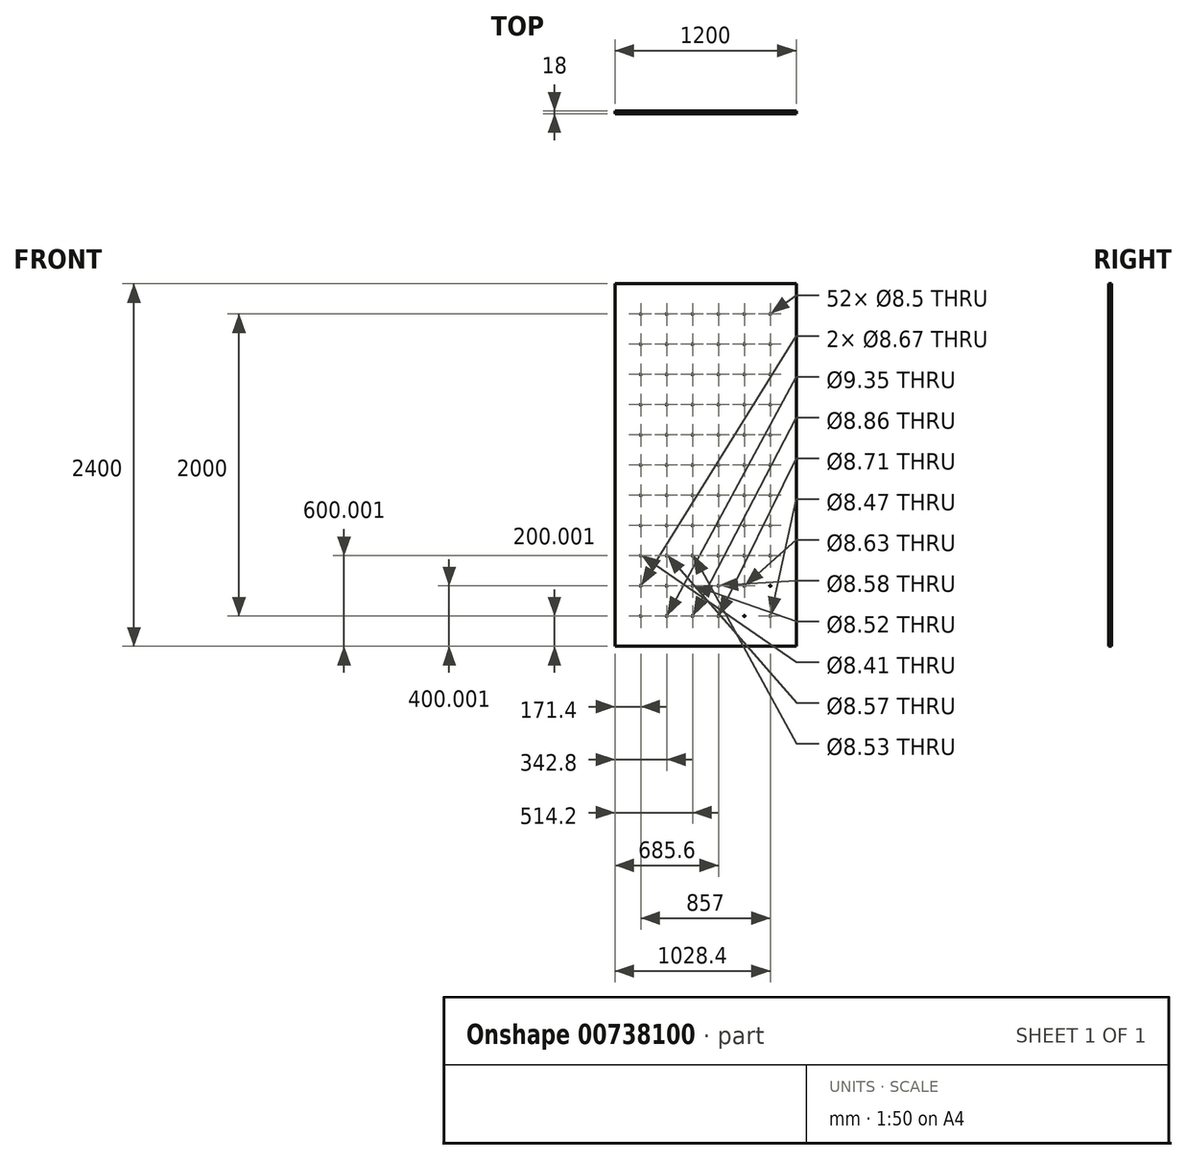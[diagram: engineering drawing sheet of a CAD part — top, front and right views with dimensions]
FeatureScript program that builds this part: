
annotation { "Feature Type Name" : "Feature", "Feature Type Description" : "" }
export const myFeature = defineFeature(function(context is Context, id is Id, definition is map)
    precondition{}
    {
        {
            var Q0;
            Q0=qCreatedBy(makeId("Front.planeOp"),FACE);
            var sketch = newSketch(context, id + "F0", { "sketchPlane" : qUnion([Q0])});
            skLineSegment(sketch, "E0.bottom", {"start": v(-600, 1570.02) * mm, "end": v(600, 1570.02) * mm});
            skLineSegment(sketch, "E0.top", {"start": v(-600, -829.98) * mm, "end": v(600, -829.98) * mm});
            skLineSegment(sketch, "E0.left", {"start": v(-600, 1570.02) * mm, "end": v(-600, -829.98) * mm});
            skLineSegment(sketch, "E0.right", {"start": v(600, 1570.02) * mm, "end": v(600, -829.98) * mm});
            skPoint(sketch, "E1", {"position": v(-428.6, 1570.02) * mm});
            skPoint(sketch, "E2", {"position": v(-257.2, 1570.02) * mm});
            skPoint(sketch, "E3", {"position": v(-85.8, 1570.02) * mm});
            skPoint(sketch, "E4", {"position": v(257, 1570.02) * mm});
            skPoint(sketch, "E5", {"position": v(428.4, 1570.02) * mm});
            skPoint(sketch, "E6", {"position": v(85.6, 1570.02) * mm});
            skPoint(sketch, "E7", {"position": v(-600, 1370.02) * mm});
            skPoint(sketch, "E8", {"position": v(-600, 1170.02) * mm});
            skPoint(sketch, "E9", {"position": v(-600, 970.02) * mm});
            skPoint(sketch, "E10", {"position": v(-600, 770.02) * mm});
            skPoint(sketch, "E11", {"position": v(-600, 570.02) * mm});
            skPoint(sketch, "E12", {"position": v(-600, 370.02) * mm});
            skPoint(sketch, "E13", {"position": v(-600, 170.02) * mm});
            skPoint(sketch, "E14", {"position": v(-600, -29.98) * mm});
            skPoint(sketch, "E15", {"position": v(-600, -229.98) * mm});
            skPoint(sketch, "E16", {"position": v(-600, -429.98) * mm});
            skPoint(sketch, "E17", {"position": v(-600, -629.98) * mm});
            skPoint(sketch, "E18.endSnap0", {"position": v(0, -829.98) * mm});
            skCircle(sketch, "E19", {"center": v(-428.6, -629.98) * mm, "radius": 4.25 * mm});
            skCircle(sketch, "E20", {"center": v(-257.2, -629.98) * mm, "radius": 4.67 * mm});
            skCircle(sketch, "E21", {"center": v(-85.8, -629.98) * mm, "radius": 4.43 * mm});
            skCircle(sketch, "E22", {"center": v(85.6, -629.98) * mm, "radius": 4.35 * mm});
            skCircle(sketch, "E23", {"center": v(257, -629.98) * mm, "radius": 4.1 * mm});
            skCircle(sketch, "E24", {"center": v(428.4, -629.98) * mm, "radius": 4.23 * mm});
            skCircle(sketch, "E25", {"center": v(428.4, -429.98) * mm, "radius": 4.2 * mm});
            skCircle(sketch, "E26", {"center": v(257, -429.98) * mm, "radius": 4.32 * mm});
            skCircle(sketch, "E27", {"center": v(85.6, -429.98) * mm, "radius": 4.29 * mm});
            skCircle(sketch, "E28", {"center": v(-85.8, -429.98) * mm, "radius": 4.26 * mm});
            skCircle(sketch, "E29", {"center": v(-257.2, -429.98) * mm, "radius": 4.33 * mm});
            skCircle(sketch, "E30", {"center": v(-428.6, -429.98) * mm, "radius": 4.33 * mm});
            skCircle(sketch, "E31", {"center": v(-428.6, -229.98) * mm, "radius": 4.2 * mm});
            skCircle(sketch, "E32", {"center": v(-257.2, -229.98) * mm, "radius": 4.29 * mm});
            skCircle(sketch, "E33", {"center": v(-85.8, -229.98) * mm, "radius": 4.26 * mm});
            skCircle(sketch, "E34", {"center": v(85.6, -229.98) * mm, "radius": 4.25 * mm});
            skCircle(sketch, "E35", {"center": v(257, -229.98) * mm, "radius": 4.25 * mm});
            skCircle(sketch, "E36", {"center": v(428.4, -229.98) * mm, "radius": 4.25 * mm});
            skCircle(sketch, "E37", {"center": v(428.4, -29.98) * mm, "radius": 4.25 * mm});
            skCircle(sketch, "E38", {"center": v(257, -29.98) * mm, "radius": 4.25 * mm});
            skCircle(sketch, "E39", {"center": v(85.6, -29.98) * mm, "radius": 4.25 * mm});
            skCircle(sketch, "E40", {"center": v(-85.8, -29.98) * mm, "radius": 4.25 * mm});
            skCircle(sketch, "E41", {"center": v(-257.2, -29.98) * mm, "radius": 4.25 * mm});
            skCircle(sketch, "E42", {"center": v(-428.6, -29.98) * mm, "radius": 4.25 * mm});
            skCircle(sketch, "E43", {"center": v(428.4, 170.02) * mm, "radius": 4.25 * mm});
            skCircle(sketch, "E44", {"center": v(257, 170.02) * mm, "radius": 4.25 * mm});
            skCircle(sketch, "E45", {"center": v(85.6, 170.02) * mm, "radius": 4.25 * mm});
            skCircle(sketch, "E46", {"center": v(-85.8, 170.02) * mm, "radius": 4.25 * mm});
            skCircle(sketch, "E47", {"center": v(-257.2, 170.02) * mm, "radius": 4.25 * mm});
            skCircle(sketch, "E48", {"center": v(-428.6, 170.02) * mm, "radius": 4.25 * mm});
            skCircle(sketch, "E49", {"center": v(-428.6, 370.02) * mm, "radius": 4.25 * mm});
            skCircle(sketch, "E50", {"center": v(-257.2, 370.02) * mm, "radius": 4.25 * mm});
            skCircle(sketch, "E51", {"center": v(-85.8, 370.02) * mm, "radius": 4.25 * mm});
            skCircle(sketch, "E52", {"center": v(85.6, 370.02) * mm, "radius": 4.25 * mm});
            skCircle(sketch, "E53", {"center": v(257, 370.02) * mm, "radius": 4.25 * mm});
            skCircle(sketch, "E54", {"center": v(428.4, 370.02) * mm, "radius": 4.25 * mm});
            skCircle(sketch, "E55", {"center": v(428.4, 570.02) * mm, "radius": 4.25 * mm});
            skCircle(sketch, "E56", {"center": v(257, 570.02) * mm, "radius": 4.25 * mm});
            skCircle(sketch, "E57", {"center": v(85.6, 570.02) * mm, "radius": 4.25 * mm});
            skCircle(sketch, "E58", {"center": v(-85.8, 570.02) * mm, "radius": 4.25 * mm});
            skCircle(sketch, "E59", {"center": v(-257.2, 570.02) * mm, "radius": 4.25 * mm});
            skCircle(sketch, "E60", {"center": v(-428.6, 570.02) * mm, "radius": 4.25 * mm});
            skCircle(sketch, "E61", {"center": v(-257.2, 770.02) * mm, "radius": 4.25 * mm});
            skCircle(sketch, "E62", {"center": v(-428.6, 770.02) * mm, "radius": 4.25 * mm});
            skCircle(sketch, "E63", {"center": v(-85.8, 770.02) * mm, "radius": 4.25 * mm});
            skCircle(sketch, "E64", {"center": v(85.6, 770.02) * mm, "radius": 4.25 * mm});
            skCircle(sketch, "E65", {"center": v(257, 770.02) * mm, "radius": 4.25 * mm});
            skCircle(sketch, "E66", {"center": v(428.4, 770.02) * mm, "radius": 4.25 * mm});
            skCircle(sketch, "E67", {"center": v(-428.6, 970.02) * mm, "radius": 4.25 * mm});
            skCircle(sketch, "E68", {"center": v(-257.2, 970.02) * mm, "radius": 4.25 * mm});
            skCircle(sketch, "E69", {"center": v(-85.8, 970.02) * mm, "radius": 4.25 * mm});
            skCircle(sketch, "E70", {"center": v(85.6, 970.02) * mm, "radius": 4.25 * mm});
            skCircle(sketch, "E71", {"center": v(257, 970.02) * mm, "radius": 4.25 * mm});
            skCircle(sketch, "E72", {"center": v(428.4, 970.02) * mm, "radius": 4.25 * mm});
            skCircle(sketch, "E73", {"center": v(428.4, 1170.02) * mm, "radius": 4.25 * mm});
            skCircle(sketch, "E74", {"center": v(257, 1170.02) * mm, "radius": 4.25 * mm});
            skCircle(sketch, "E75", {"center": v(85.6, 1170.02) * mm, "radius": 4.25 * mm});
            skCircle(sketch, "E76", {"center": v(-85.8, 1170.02) * mm, "radius": 4.25 * mm});
            skCircle(sketch, "E77", {"center": v(-257.2, 1170.02) * mm, "radius": 4.25 * mm});
            skCircle(sketch, "E78", {"center": v(-428.6, 1170.02) * mm, "radius": 4.25 * mm});
            skCircle(sketch, "E79", {"center": v(-428.6, 1370.02) * mm, "radius": 4.25 * mm});
            skCircle(sketch, "E80", {"center": v(-257.2, 1370.02) * mm, "radius": 4.25 * mm});
            skCircle(sketch, "E81", {"center": v(-85.8, 1370.02) * mm, "radius": 4.25 * mm});
            skCircle(sketch, "E82", {"center": v(85.6, 1370.02) * mm, "radius": 4.25 * mm});
            skCircle(sketch, "E83", {"center": v(257, 1370.02) * mm, "radius": 4.25 * mm});
            skCircle(sketch, "E84", {"center": v(428.4, 1370.02) * mm, "radius": 4.25 * mm});
            skSolve(sketch);
        }
        {
            var Q0;
            Q0=makeQuery(id+"F0.imprint","IMPRINT",FACE,{"disambiguationData":[TD([[makeQuery(id+"F0.imprint","IMPRINT",EDGE,{"derivedFrom":sQuery(id+"F0.wireOp",EDGE,"E0.bottom")}),-1.0]])]});
            extrude(context, id + "F1", {"entities" : qUnion([Q0]), "depth" : 18 * mm, "offsetDistance" : 25 * mm});
        }
    });
